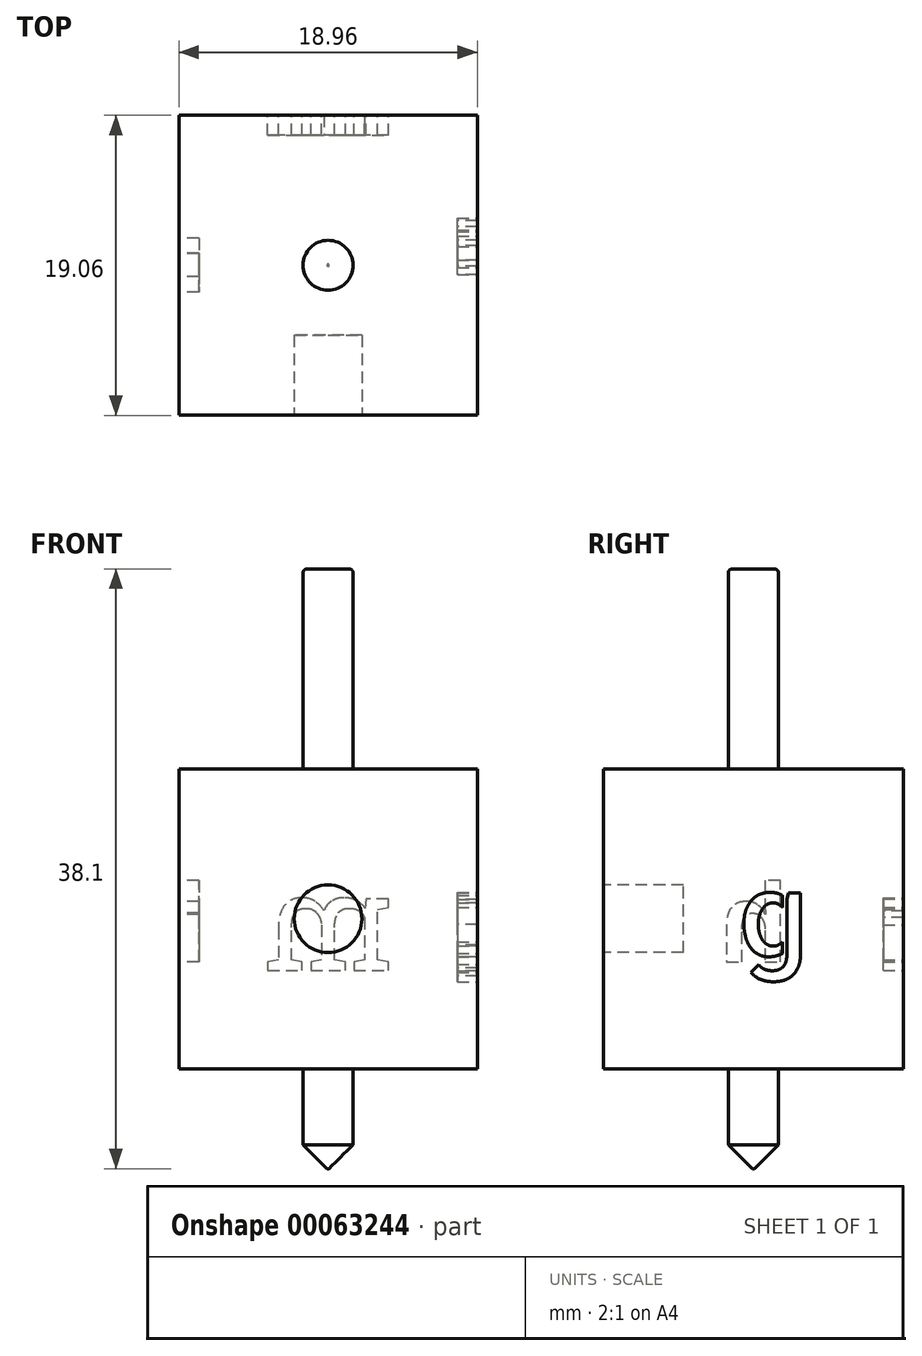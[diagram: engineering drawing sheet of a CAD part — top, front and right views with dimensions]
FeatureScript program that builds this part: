
annotation { "Feature Type Name" : "Feature", "Feature Type Description" : "" }
export const myFeature = defineFeature(function(context is Context, id is Id, definition is map)
    precondition{}
    {
        {
            var Q0;
            Q0=qCreatedBy(makeId("Top.planeOp"),FACE);
            var sketch = newSketch(context, id + "F0", { "sketchPlane" : qUnion([Q0])});
            skLineSegment(sketch, "E0.rect.bottom", {"start": v(9.48, 9.53) * mm, "end": v(-9.48, 9.53) * mm});
            skLineSegment(sketch, "E0.rect.top", {"start": v(9.48, -9.53) * mm, "end": v(-9.48, -9.53) * mm});
            skLineSegment(sketch, "E0.rect.left", {"start": v(9.48, 9.53) * mm, "end": v(9.48, -9.53) * mm});
            skLineSegment(sketch, "E0.rect.right", {"start": v(-9.48, 9.53) * mm, "end": v(-9.48, -9.53) * mm});
            skPoint(sketch, "E0.rect.middle", {"position": v(0, 0) * mm});
            skSolve(sketch);
        }
        {
            var Q0;
            Q0=qCreatedBy(makeId("Top.planeOp"),FACE);
            var sketch = newSketch(context, id + "F1", { "sketchPlane" : qUnion([Q0])});
            skCircle(sketch, "E1", {"center": v(0, 0) * mm, "radius": 1.59 * mm});
            skSolve(sketch);
        }
        {
            var Q0;
            Q0=makeQuery(id+"F0.imprint","IMPRINT",FACE,{"disambiguationData":[TD([[makeQuery(id+"F0.imprint","IMPRINT",EDGE,{"derivedFrom":sQuery(id+"F0.wireOp",EDGE,"E0.rect.bottom")}),1.0]])]});
            extrude(context, id + "F2", {"entities" : qUnion([Q0]), "depth" : 19.05 * mm});
        }
        {
            var Q0;
            Q0=makeQuery(id+"F2.opExtrude","SWEPT_FACE",FACE,{"disambiguationData":[OSD([sQuery(id+"F0.wireOp",EDGE,"E0.rect.left")])]});
            var sketch = newSketch(context, id + "F3", { "sketchPlane" : qUnion([Q0])});
            skText(sketch, "E2", { "text": "g", "fontName": "AllertaStencil-Regular.ttf"});
            const initialGuessF3  = {"E2": [-0.00109, 0.00714, 1, 0, 0.00526]};
            skSetInitialGuess(sketch, initialGuessF3);
            skSolve(sketch);
        }
        {
            var Q0;
            Q0=makeQuery(id+"F2.opExtrude","SWEPT_FACE",FACE,{"disambiguationData":[OSD([sQuery(id+"F0.wireOp",EDGE,"E0.rect.bottom")])]});
            var sketch = newSketch(context, id + "F4", { "sketchPlane" : qUnion([Q0])});
            skText(sketch, "E3", { "text": "m", "fontName": "RobotoSlab-Regular.ttf"});
            const initialGuessF4  = {"E3": [-0.00404, 0.00625, 1, 0, 0.00617]};
            skSetInitialGuess(sketch, initialGuessF4);
            skSolve(sketch);
        }
        {
            var Q0;
            Q0=makeQuery(id+"F2.opExtrude","SWEPT_FACE",FACE,{"disambiguationData":[OSD([sQuery(id+"F0.wireOp",EDGE,"E0.rect.right")])]});
            var sketch = newSketch(context, id + "F5", { "sketchPlane" : qUnion([Q0])});
            skText(sketch, "E4", { "text": "h", "fontName": "Arimo-Bold.ttf"});
            const initialGuessF5  = {"E4": [-0.00222, 0.00678, 1, 0, 0.00514]};
            skSetInitialGuess(sketch, initialGuessF5);
            skSolve(sketch);
        }
        {
            var Q0;
            Q0=makeQuery(id+"F2.opExtrude","SWEPT_FACE",FACE,{"disambiguationData":[OSD([sQuery(id+"F0.wireOp",EDGE,"E0.rect.top")])]});
            var sketch = newSketch(context, id + "F6", { "sketchPlane" : qUnion([Q0])});
            skCircle(sketch, "E5", {"center": v(0, 9.53) * mm, "radius": 2.15 * mm});
            skPoint(sketch, "E5.centerSnap0", {"position": v(-9.48, 9.53) * mm});
            skSolve(sketch);
        }
        {
            var Q0;
            Q0=makeQuery(id+"F6.imprint","IMPRINT",FACE,{"disambiguationData":[TD([[makeQuery(id+"F6.imprint","IMPRINT",EDGE,{"derivedFrom":sQuery(id+"F6.wireOp",EDGE,"E5")}),1.0]])]});
            extrude(context, id + "F7", {"entities" : qUnion([Q0]), "operationType" : NewBodyOperationType.REMOVE, "oppositeDirection" : true, "depth" : 5.08 * mm});
        }
        {
            var Q0;
            Q0 = qSketchRegion(id + "F3", true);
            extrude(context, id + "F8", {"entities" : qUnion([Q0]), "operationType" : NewBodyOperationType.REMOVE, "oppositeDirection" : true, "depth" : 1.27 * mm});
        }
        {
            var Q0;
            Q0 = qSketchRegion(id + "F4", true);
            extrude(context, id + "F9", {"entities" : qUnion([Q0]), "operationType" : NewBodyOperationType.REMOVE, "oppositeDirection" : true, "depth" : 1.27 * mm});
        }
        {
            var Q0;
            Q0 = qSketchRegion(id + "F5", true);
            extrude(context, id + "F10", {"entities" : qUnion([Q0]), "operationType" : NewBodyOperationType.REMOVE, "oppositeDirection" : true, "depth" : 1.27 * mm});
        }
        {
            var Q0;
            Q0=makeQuery(id+"F1.imprint","IMPRINT",FACE,{"disambiguationData":[TD([[makeQuery(id+"F1.imprint","IMPRINT",EDGE,{"derivedFrom":sQuery(id+"F1.wireOp",EDGE,"E1")}),1.0]])]});
            extrude(context, id + "F11", {"entities" : qUnion([Q0]), "operationType" : NewBodyOperationType.REMOVE, "endBound" : BoundingType.THROUGH_ALL, "depth" : 25.4 * mm});
        }
        {
            var Q0;
            Q0=makeQuery(id+"F2.opExtrude","CAP_FACE",FACE,{"disambiguationData":[OSD([sQuery(id+"F0.wireOp",EDGE,"E0.rect.bottom"),sQuery(id+"F0.wireOp",EDGE,"E0.rect.top"),sQuery(id+"F0.wireOp",EDGE,"E0.rect.left"),sQuery(id+"F0.wireOp",EDGE,"E0.rect.right")])],"isStart":false});
            var sketch = newSketch(context, id + "F12", { "sketchPlane" : qUnion([Q0])});
            skCircle(sketch, "E6", {"center": v(0, 0) * mm, "radius": 1.64 * mm});
            skSolve(sketch);
        }
        {
            var Q0;
            Q0=makeQuery(id+"F12.imprint","IMPRINT",FACE,{"disambiguationData":[TD([[makeQuery(id+"F12.imprint","IMPRINT",EDGE,{"derivedFrom":makeQuery(id+"F11.boolean.opBoolean","INTERSECT",EDGE,{"derivedFrom":[makeQuery(id+"F2.opExtrude","CAP_FACE",FACE,{"disambiguationData":[OSD([sQuery(id+"F0.wireOp",EDGE,"E0.rect.bottom"),sQuery(id+"F0.wireOp",EDGE,"E0.rect.top"),sQuery(id+"F0.wireOp",EDGE,"E0.rect.left"),sQuery(id+"F0.wireOp",EDGE,"E0.rect.right")])],"isStart":false}),makeQuery(id+"F11.opExtrude","SWEPT_FACE",FACE,{"disambiguationData":[OSD([sQuery(id+"F1.wireOp",EDGE,"E1")])]})]})}),-1.0]])]});
            extrude(context, id + "F13", {"entities" : qUnion([Q0]), "operationType" : NewBodyOperationType.ADD, "depth" : 12.7 * mm, "hasSecondDirection" : true, "secondDirectionOppositeDirection" : true, "secondDirectionDepth" : 25.4 * mm});
        }
        {
            var Q0;
            Q0=makeQuery(id+"F13.opExtrude","CAP_FACE",FACE,{"disambiguationData":[OSD([sQuery(id+"F0.wireOp",EDGE,"E0.rect.bottom"),sQuery(id+"F0.wireOp",EDGE,"E0.rect.top"),sQuery(id+"F0.wireOp",EDGE,"E0.rect.left"),sQuery(id+"F0.wireOp",EDGE,"E0.rect.right"),sQuery(id+"F1.wireOp",EDGE,"E1")])],"isStart":true});
            chamfer(context, id + "F14", {"entities" : qUnion([Q0]), "width" : 1.52 * mm, "tangentPropagation" : true});
        }
        {
            var Q0;
            Q0=makeQuery(id+"F13.opExtrude","CAP_EDGE",EDGE,{"disambiguationData":[OSD([sQuery(id+"F0.wireOp",EDGE,"E0.rect.bottom"),sQuery(id+"F0.wireOp",EDGE,"E0.rect.top"),sQuery(id+"F0.wireOp",EDGE,"E0.rect.left"),sQuery(id+"F0.wireOp",EDGE,"E0.rect.right"),sQuery(id+"F1.wireOp",EDGE,"E1")])],"isStart":false});
            fillet(context, id + "F15", {"entities" : qUnion([Q0]), "radius" : 0.25 * mm, "tangentPropagation" : true, "allowEdgeOverflow" : false});
        }
    });
